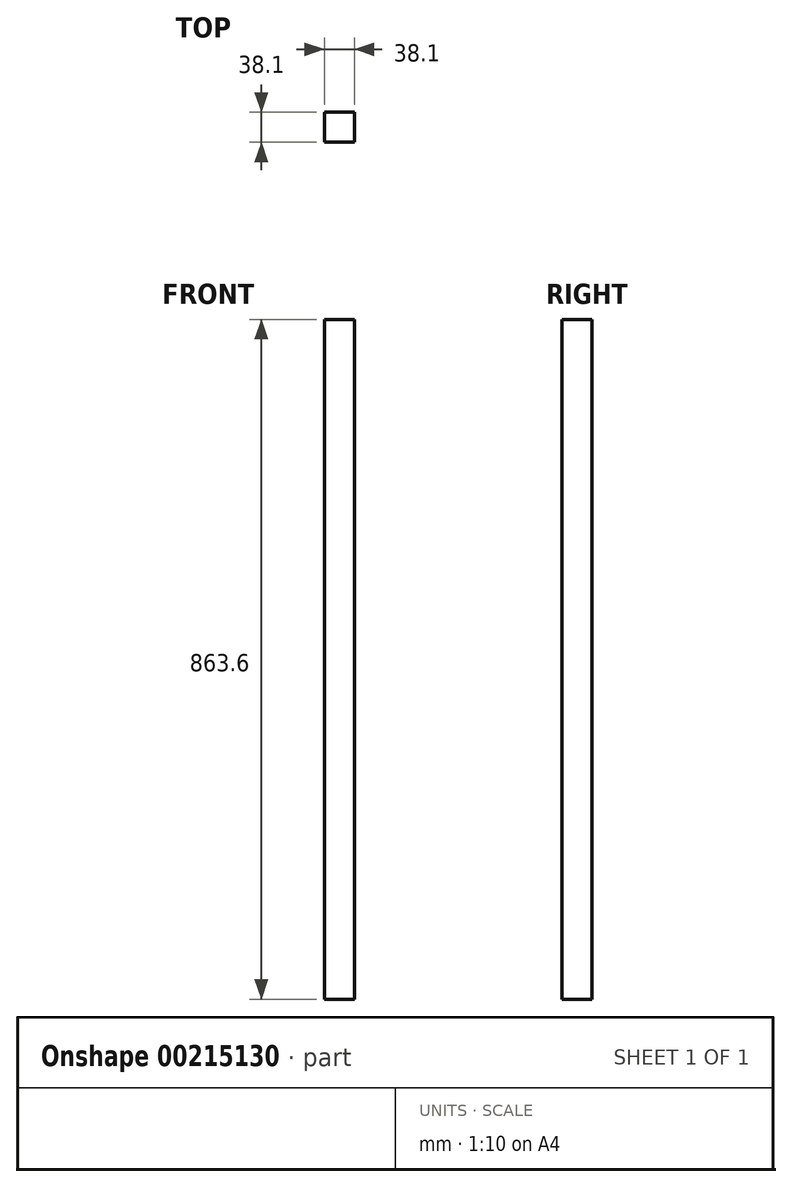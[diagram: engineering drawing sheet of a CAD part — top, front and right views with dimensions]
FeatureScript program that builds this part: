
annotation { "Feature Type Name" : "Feature", "Feature Type Description" : "" }
export const myFeature = defineFeature(function(context is Context, id is Id, definition is map)
    precondition{}
    {
        {
            var Q0;
            Q0=qCreatedBy(makeId("Top.planeOp"),FACE);
            var sketch = newSketch(context, id + "F0", { "sketchPlane" : qUnion([Q0])});
            skLineSegment(sketch, "E0.bottom", {"start": v(0, 0) * mm, "end": v(38.1, 0) * mm});
            skLineSegment(sketch, "E0.top", {"start": v(0, 38.1) * mm, "end": v(38.1, 38.1) * mm});
            skLineSegment(sketch, "E0.left", {"start": v(0, 0) * mm, "end": v(0, 38.1) * mm});
            skLineSegment(sketch, "E0.right", {"start": v(38.1, 0) * mm, "end": v(38.1, 38.1) * mm});
            skSolve(sketch);
        }
        {
            var Q0;
            Q0=makeQuery(id+"F0.imprint","IMPRINT",FACE,{"disambiguationData":[TD([[makeQuery(id+"F0.imprint","IMPRINT",EDGE,{"derivedFrom":sQuery(id+"F0.wireOp",EDGE,"E0.bottom")}),1.0]])]});
            extrude(context, id + "F1", {"entities" : qUnion([Q0]), "depth" : 863.6 * mm, "offsetDistance" : 25.4 * mm});
        }
    });
